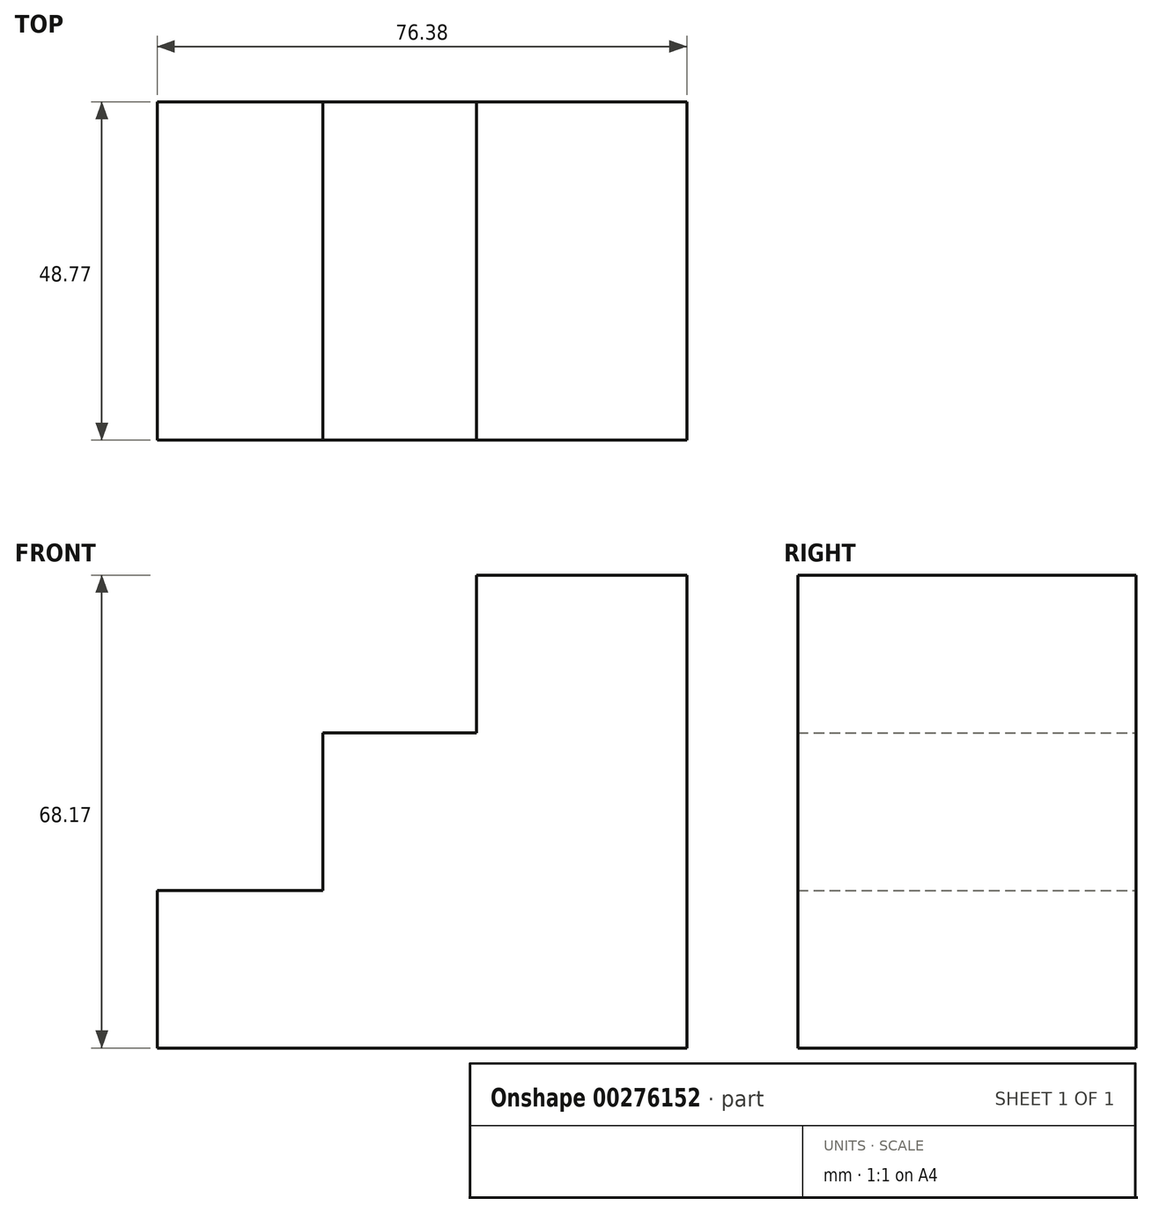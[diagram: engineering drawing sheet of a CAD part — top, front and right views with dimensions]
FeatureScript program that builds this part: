
annotation { "Feature Type Name" : "Feature", "Feature Type Description" : "" }
export const myFeature = defineFeature(function(context is Context, id is Id, definition is map)
    precondition{}
    {
        {
            var Q0;
            Q0=qCreatedBy(makeId("Front.planeOp"),FACE);
            var sketch = newSketch(context, id + "F0", { "sketchPlane" : qUnion([Q0])});
            skLineSegment(sketch, "E0", {"start": v(0, 0) * mm, "end": v(-76.38, 0) * mm});
            skLineSegment(sketch, "E1", {"start": v(-76.38, 0) * mm, "end": v(-76.38, 22.72) * mm});
            skLineSegment(sketch, "E2", {"start": v(-76.38, 22.72) * mm, "end": v(-52.51, 22.72) * mm});
            skLineSegment(sketch, "E3", {"start": v(-52.51, 22.72) * mm, "end": v(-52.51, 45.45) * mm});
            skLineSegment(sketch, "E4", {"start": v(-52.51, 45.45) * mm, "end": v(-30.36, 45.45) * mm});
            skLineSegment(sketch, "E5", {"start": v(-30.36, 45.45) * mm, "end": v(-30.36, 68.17) * mm});
            skLineSegment(sketch, "E6", {"start": v(-30.36, 68.17) * mm, "end": v(0, 68.17) * mm});
            skLineSegment(sketch, "E7", {"start": v(0, 68.17) * mm, "end": v(0, 0) * mm});
            skSolve(sketch);
        }
        {
            var Q0;
            Q0 = qSketchRegion(id + "F0", true);
            extrude(context, id + "F1", {"entities" : qUnion([Q0]), "depth" : 48.77 * mm});
        }
    });
